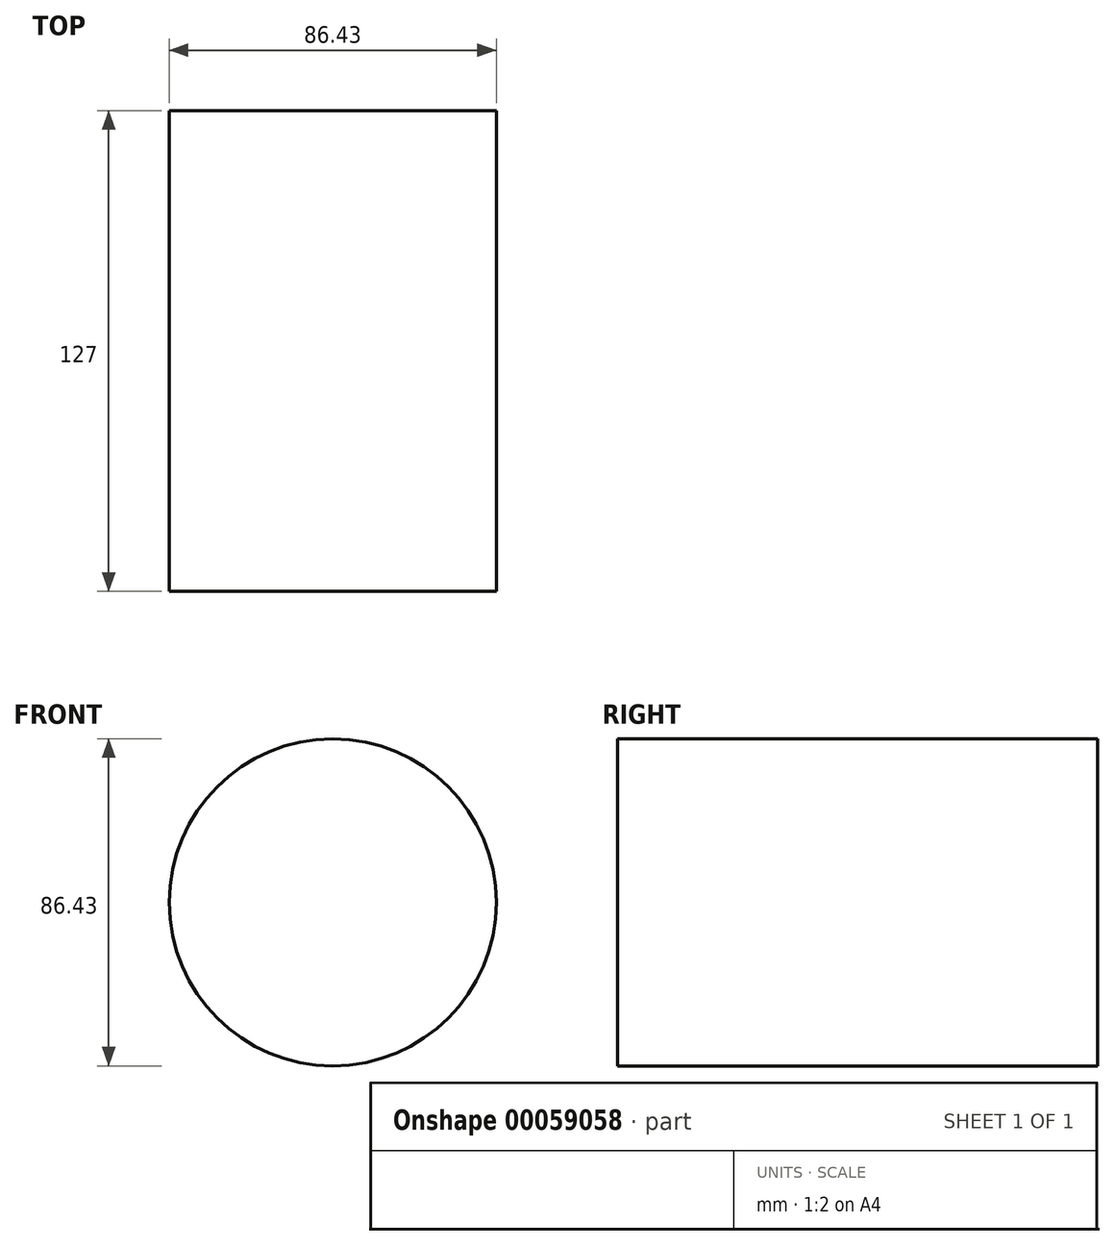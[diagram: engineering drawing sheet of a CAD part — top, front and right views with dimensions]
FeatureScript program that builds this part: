
annotation { "Feature Type Name" : "Feature", "Feature Type Description" : "" }
export const myFeature = defineFeature(function(context is Context, id is Id, definition is map)
    precondition{}
    {
        {
            var Q0;
            Q0=qCreatedBy(makeId("Top.planeOp"),FACE);
            var sketch = newSketch(context, id + "F0", { "sketchPlane" : qUnion([Q0])});
            skLineSegment(sketch, "E0.bottom", {"start": v(0, 0) * mm, "end": v(23.88, 0) * mm});
            skLineSegment(sketch, "E0.top", {"start": v(0, -22.35) * mm, "end": v(23.88, -22.35) * mm});
            skLineSegment(sketch, "E0.left", {"start": v(0, 0) * mm, "end": v(0, -22.35) * mm});
            skLineSegment(sketch, "E0.right", {"start": v(23.88, 0) * mm, "end": v(23.88, -22.35) * mm});
            skSolve(sketch);
        }
        {
            var Q0;
            Q0=makeQuery(id+"F0.imprint","IMPRINT",FACE,{"disambiguationData":[TD([[makeQuery(id+"F0.imprint","IMPRINT",EDGE,{"derivedFrom":sQuery(id+"F0.wireOp",EDGE,"E0.bottom")}),-1.0]])]});
            extrude(context, id + "F1", {"entities" : qUnion([Q0]), "depth" : 31.75 * mm});
        }
        {
            var Q0;
            Q0=makeQuery(id+"F1.opExtrude","CAP_FACE",FACE,{"disambiguationData":[OSD([sQuery(id+"F0.wireOp",EDGE,"E0.bottom"),sQuery(id+"F0.wireOp",EDGE,"E0.top"),sQuery(id+"F0.wireOp",EDGE,"E0.left"),sQuery(id+"F0.wireOp",EDGE,"E0.right")])],"isStart":false});
            var sketch = newSketch(context, id + "F2", { "sketchPlane" : qUnion([Q0])});
            skCircle(sketch, "E1", {"center": v(1.42, -1.36) * mm, "radius": 0.78 * mm});
            skCircle(sketch, "E2", {"center": v(22.54, -1.49) * mm, "radius": 0.8 * mm});
            skCircle(sketch, "E3", {"center": v(1.39, -21.13) * mm, "radius": 0.92 * mm});
            skCircle(sketch, "E4", {"center": v(22.64, -21.08) * mm, "radius": 0.86 * mm});
            skSolve(sketch);
        }
        {
            var Q0;
            Q0=makeQuery(id+"F2.imprint","IMPRINT",FACE,{"disambiguationData":[TD([[makeQuery(id+"F2.imprint","IMPRINT",EDGE,{"derivedFrom":sQuery(id+"F2.wireOp",EDGE,"E2")}),1.0]])]});
            extrude(context, id + "F3", {"entities" : qUnion([Q0]), "operationType" : NewBodyOperationType.REMOVE, "oppositeDirection" : true, "depth" : 25.4 * mm});
        }
        {
            var Q0;
            Q0=makeQuery(id+"F1.opExtrude","CAP_FACE",FACE,{"disambiguationData":[OSD([sQuery(id+"F0.wireOp",EDGE,"E0.bottom"),sQuery(id+"F0.wireOp",EDGE,"E0.top"),sQuery(id+"F0.wireOp",EDGE,"E0.left"),sQuery(id+"F0.wireOp",EDGE,"E0.right")])],"isStart":false});
            var sketch = newSketch(context, id + "F4", { "sketchPlane" : qUnion([Q0])});
            skSolve(sketch);
        }
        {
            var Q0;
            Q0=makeQuery(id+"F4.imprint","IMPRINT",FACE,{"disambiguationData":[TD([[makeQuery(id+"F4.imprint","IMPRINT",EDGE,{"derivedFrom":makeQuery(id+"F1.opExtrude","CAP_EDGE",EDGE,{"disambiguationData":[OSD([sQuery(id+"F0.wireOp",EDGE,"E0.bottom")])],"isStart":false})}),-1.0]])]});
            var sketch = newSketch(context, id + "F5", { "sketchPlane" : qUnion([Q0])});
            skCircle(sketch, "E5", {"center": v(1.07, -1.2) * mm, "radius": 0.84 * mm});
            skSolve(sketch);
        }
        {
            var Q0;
            Q0 = qSketchRegion(id + "F5", true);
            extrude(context, id + "F6", {"entities" : qUnion([Q0]), "operationType" : NewBodyOperationType.REMOVE, "oppositeDirection" : true, "depth" : 6.35 * mm});
        }
        {
            var Q0;
            Q0=makeQuery(id+"F4.imprint","IMPRINT",FACE,{"disambiguationData":[TD([[makeQuery(id+"F4.imprint","IMPRINT",EDGE,{"derivedFrom":makeQuery(id+"F1.opExtrude","CAP_EDGE",EDGE,{"disambiguationData":[OSD([sQuery(id+"F0.wireOp",EDGE,"E0.bottom")])],"isStart":false})}),-1.0]])]});
            var sketch = newSketch(context, id + "F7", { "sketchPlane" : qUnion([Q0])});
            skCircle(sketch, "E6", {"center": v(1, -21.28) * mm, "radius": 0.8 * mm});
            skSolve(sketch);
        }
        {
            var Q0;
            Q0 = qSketchRegion(id + "F7", true);
            var Q1;
            Q1=makeQuery(id+"F4.imprint","IMPRINT",FACE,{"disambiguationData":[TD([[makeQuery(id+"F4.imprint","IMPRINT",EDGE,{"derivedFrom":makeQuery(id+"F1.opExtrude","CAP_EDGE",EDGE,{"disambiguationData":[OSD([sQuery(id+"F0.wireOp",EDGE,"E0.bottom")])],"isStart":false})}),-1.0]])]});
            extrude(context, id + "F8", {"entities" : qUnion([Q0, Q1]), "operationType" : NewBodyOperationType.REMOVE, "oppositeDirection" : true, "depth" : 6.35 * mm});
        }
        {
            var Q0;
            Q0=qCreatedBy(makeId("Front.planeOp"),FACE);
            var sketch = newSketch(context, id + "F9", { "sketchPlane" : qUnion([Q0])});
            skCircle(sketch, "E7", {"center": v(32.05, 29) * mm, "radius": 43.22 * mm});
            skPoint(sketch, "E7.first.point", {"position": v(0, 0) * mm});
            skPoint(sketch, "E7.second.point", {"position": v(64.1, 0) * mm});
            skPoint(sketch, "E7.third.point", {"position": v(52.89, 66.85) * mm});
            skSolve(sketch);
        }
        {
            var Q0;
            Q0=makeQuery(id+"F9.imprint","IMPRINT",FACE,{"disambiguationData":[TD([[makeQuery(id+"F9.imprint","IMPRINT",EDGE,{"derivedFrom":sQuery(id+"F9.wireOp",EDGE,"E7")}),1.0]])]});
            extrude(context, id + "F10", {"entities" : qUnion([Q0]), "operationType" : NewBodyOperationType.ADD, "depth" : 127 * mm});
        }
    });
